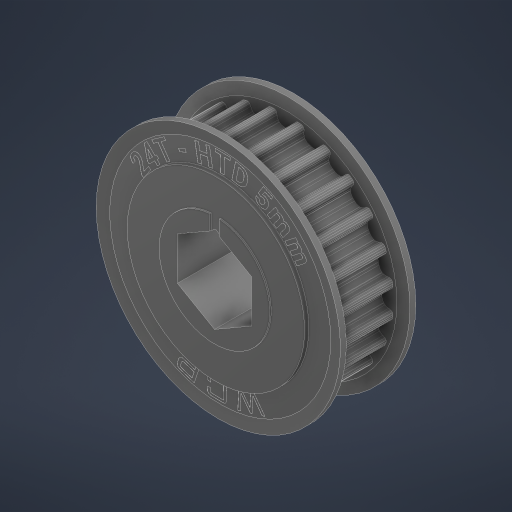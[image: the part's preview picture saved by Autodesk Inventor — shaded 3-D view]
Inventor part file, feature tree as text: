
AUTODESK INVENTOR PART (.ipt)
format: ipt  version: 2024 (Build 280153000, 153)  size: 938,496 bytes
history: native  units: in
note: dims shown in document units (in); Inventor stores cm internally (conversion verified against a paired STEP export)
features: mirror x2, other x1
ambient origin geometry x8: Origin, YZ Plane, XZ Plane, XY Plane, X Axis, Y Axis, Z Axis, Center Point
bodies: Solid1 (feature_tree), Solid2 (feature_tree), Solid3 (feature_tree)
feature tree (3):
  mirror  "Mirror2"
  mirror  "Mirror1"
  other  "Cut-Extrude5"
